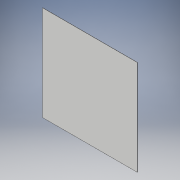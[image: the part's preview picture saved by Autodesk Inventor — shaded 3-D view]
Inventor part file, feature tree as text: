
AUTODESK INVENTOR PART (.ipt)
format: ipt  version: 2019 (Build 230136000, 136)  size: 89,600 bytes
history: native  units: in
note: dims shown in document units (in); Inventor stores cm internally (conversion verified against a paired STEP export)
features: other x1, extrude x1, sketch x1
ambient origin geometry x8: Origin, YZ Plane, XZ Plane, XY Plane, X Axis, Y Axis, Z Axis, Center Point
bodies: Body1 (feature_tree)
feature tree (3):
  other  "Galvanized steel sheet"
  extrude  "Extrusion1"  Depth=60.0in
  sketch  "Sketch1"  dims[d0=59.784in d1=60.0in d2=0.108in d3=0.0in]
